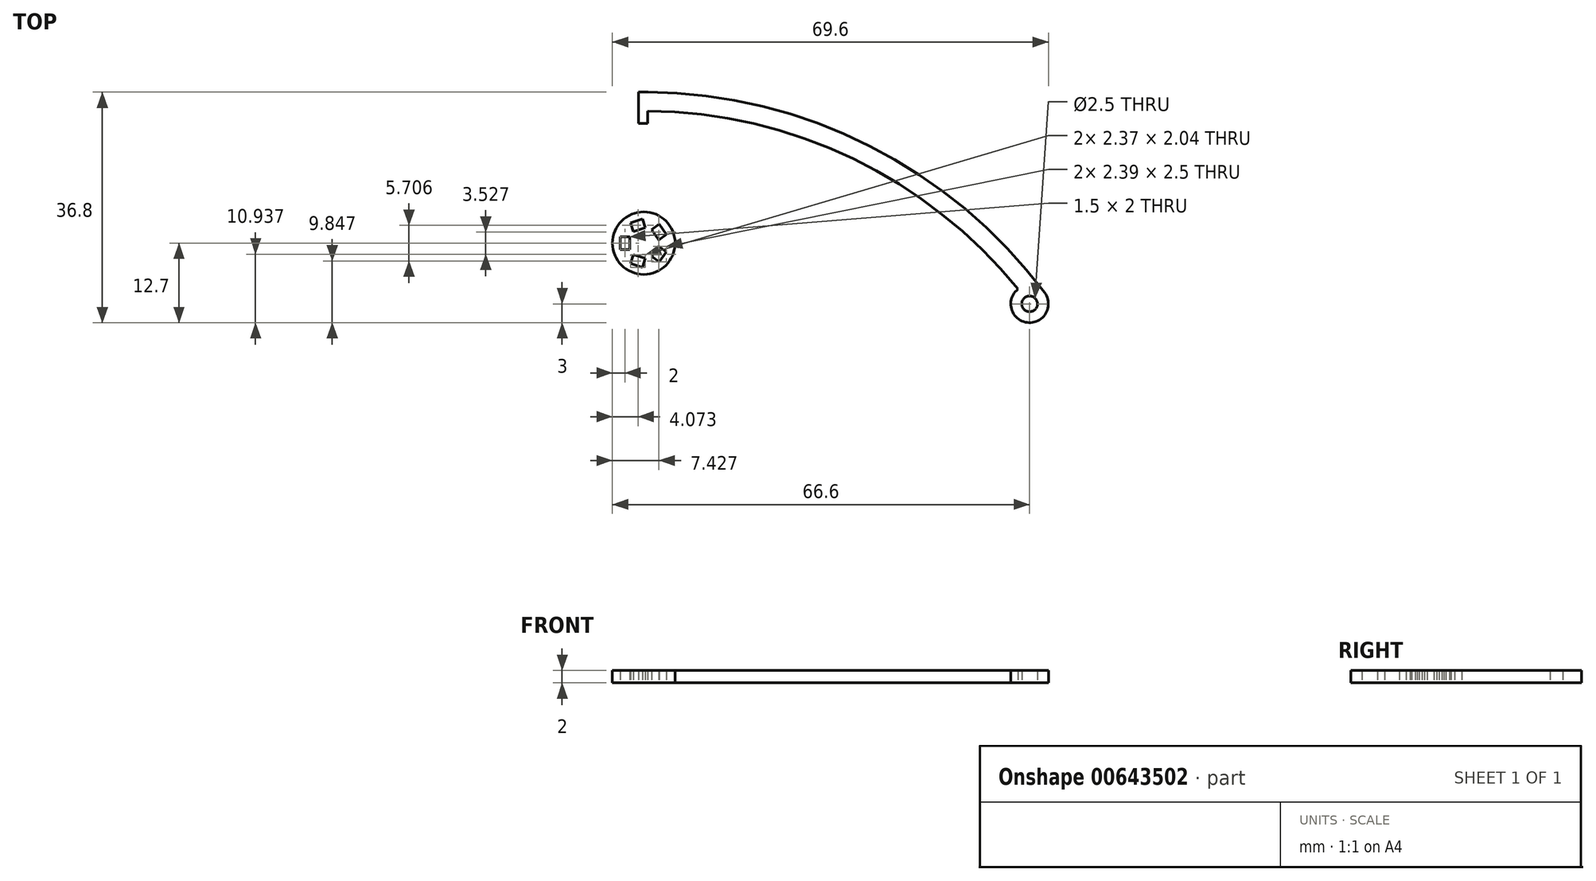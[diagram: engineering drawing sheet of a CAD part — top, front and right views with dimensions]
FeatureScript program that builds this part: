
annotation { "Feature Type Name" : "Feature", "Feature Type Description" : "" }
export const myFeature = defineFeature(function(context is Context, id is Id, definition is map)
    precondition{}
    {
        {
            var Q0;
            Q0=qCreatedBy(makeId("Top.planeOp"),FACE);
            var sketch = newSketch(context, id + "F0", { "sketchPlane" : qUnion([Q0])});
            skLineSegment(sketch, "E0", {"start": v(0.64, -3) * mm, "end": v(0.64, -5) * mm});
            skLineSegment(sketch, "E1", {"start": v(0.64, -5) * mm, "end": v(-0.86, -5) * mm});
            skLineSegment(sketch, "E2", {"start": v(-0.86, -5) * mm, "end": v(-0.86, 0) * mm});
            skArc(sketch, "E3.0", {"start": v(64, -32) * mm, "mid": v(36.07, -8.6) * mm, "end": v(0.66, 0) * mm});
            skCircle(sketch, "E4", {"center": v(61.6, -33.8) * mm, "radius": 1.25 * mm});
            skArc(sketch, "E5", {"start": v(59.75, -31.44) * mm, "mid": v(61.2, -36.77) * mm, "end": v(64, -32) * mm});
            skArc(sketch, "E6.trimOffspring", {"start": v(59.75, -31.44) * mm, "mid": v(33.37, -10.6) * mm, "end": v(0.64, -3) * mm});
            skLineSegment(sketch, "E7", {"start": v(-0.86, 0) * mm, "end": v(0.66, 0) * mm});
            skSolve(sketch);
        }
        {
            var Q0;
            Q0 = qSketchRegion(id + "F0", true);
            extrude(context, id + "F1", {"entities" : qUnion([Q0]), "depth" : 2 * mm, "offsetDistance" : 25 * mm});
        }
        {
            var Q0;
            Q0=qCreatedBy(makeId("Top.planeOp"),FACE);
            var sketch = newSketch(context, id + "F2", { "sketchPlane" : qUnion([Q0])});
            skCircle(sketch, "E8", {"center": v(0, 0) * mm, "radius": 5 * mm});
            skLineSegment(sketch, "E9.bottom", {"start": v(-2.25, -1) * mm, "end": v(-3.75, -1) * mm});
            skLineSegment(sketch, "E9.top", {"start": v(-2.25, 1) * mm, "end": v(-3.75, 1) * mm});
            skLineSegment(sketch, "E9.left", {"start": v(-2.25, -1) * mm, "end": v(-2.25, 1) * mm});
            skLineSegment(sketch, "E9.right", {"start": v(-3.75, -1) * mm, "end": v(-3.75, 1) * mm});
            skPoint(sketch, "E9.middle", {"position": v(-3, 0) * mm});
            skLineSegment(sketch, "E10.1.0", {"start": v(-0.2, -3.88) * mm, "end": v(-2.1, -3.26) * mm});
            skLineSegment(sketch, "E10.1.1", {"start": v(0.26, -2.45) * mm, "end": v(-1.65, -1.83) * mm});
            skLineSegment(sketch, "E10.1.2", {"start": v(-1.65, -1.83) * mm, "end": v(-2.1, -3.26) * mm});
            skLineSegment(sketch, "E10.1.3", {"start": v(0.26, -2.45) * mm, "end": v(-0.2, -3.88) * mm});
            skPoint(sketch, "E10.1.4", {"position": v(-0.93, -2.85) * mm});
            skLineSegment(sketch, "E10.2.0", {"start": v(3.62, -1.4) * mm, "end": v(2.45, -3.01) * mm});
            skLineSegment(sketch, "E10.2.1", {"start": v(2.4, -0.51) * mm, "end": v(1.23, -2.13) * mm});
            skLineSegment(sketch, "E10.2.2", {"start": v(1.23, -2.13) * mm, "end": v(2.45, -3.01) * mm});
            skLineSegment(sketch, "E10.2.3", {"start": v(2.4, -0.51) * mm, "end": v(3.62, -1.4) * mm});
            skPoint(sketch, "E10.2.4", {"position": v(2.43, -1.76) * mm});
            skLineSegment(sketch, "E10.3.0", {"start": v(2.45, 3.01) * mm, "end": v(3.62, 1.4) * mm});
            skLineSegment(sketch, "E10.3.1", {"start": v(1.23, 2.13) * mm, "end": v(2.4, 0.51) * mm});
            skLineSegment(sketch, "E10.3.2", {"start": v(2.4, 0.51) * mm, "end": v(3.62, 1.4) * mm});
            skLineSegment(sketch, "E10.3.3", {"start": v(1.23, 2.13) * mm, "end": v(2.45, 3.01) * mm});
            skPoint(sketch, "E10.3.4", {"position": v(2.43, 1.76) * mm});
            skLineSegment(sketch, "E10.4.0", {"start": v(-2.1, 3.26) * mm, "end": v(-0.2, 3.88) * mm});
            skLineSegment(sketch, "E10.4.1", {"start": v(-1.65, 1.83) * mm, "end": v(0.26, 2.45) * mm});
            skLineSegment(sketch, "E10.4.2", {"start": v(0.26, 2.45) * mm, "end": v(-0.2, 3.88) * mm});
            skLineSegment(sketch, "E10.4.3", {"start": v(-1.65, 1.83) * mm, "end": v(-2.1, 3.26) * mm});
            skPoint(sketch, "E10.4.4", {"position": v(-0.93, 2.85) * mm});
            skSolve(sketch);
        }
        {
            var Q0;
            Q0 = qSketchRegion(id + "F2", true);
            extrude(context, id + "F3", {"entities" : qUnion([Q0]), "depth" : 2 * mm, "offsetDistance" : 25 * mm});
        }
        {
            var Q0;
            Q0=makeQuery(id+"F1.opExtrude","SWEPT_BODY",BODY,{"disambiguationData":[OSD([sQuery(id+"F0.wireOp",EDGE,"ciyF9gMq-OtOg-31Ct-fEZP-9Z6uuP33LbPV"),sQuery(id+"F0.wireOp",EDGE,"1b6d1320-dbbd-447f-8786-3a0c2fdd63cb.0"),sQuery(id+"F0.wireOp",EDGE,"E0"),sQuery(id+"F0.wireOp",EDGE,"E1"),sQuery(id+"F0.wireOp",EDGE,"E2"),sQuery(id+"F0.wireOp",EDGE,"e6jzngCc-pjHB-Q8lV-RtdD-TbqlkxrzJ0p0"),sQuery(id+"F0.wireOp",EDGE,"U6AuzwBb-cHqz-hfWc-qJq7-8mlStpsWz9Do")])]});
            transform(context, id + "F4", {"entities" : qUnion([Q0]), "transformType" : TransformType.TRANSLATION_3D, "dx" : 0 * mm, "dy" : 24.1 * mm, "dz" : 0 * mm, "makeCopy" : false});
        }
    });
